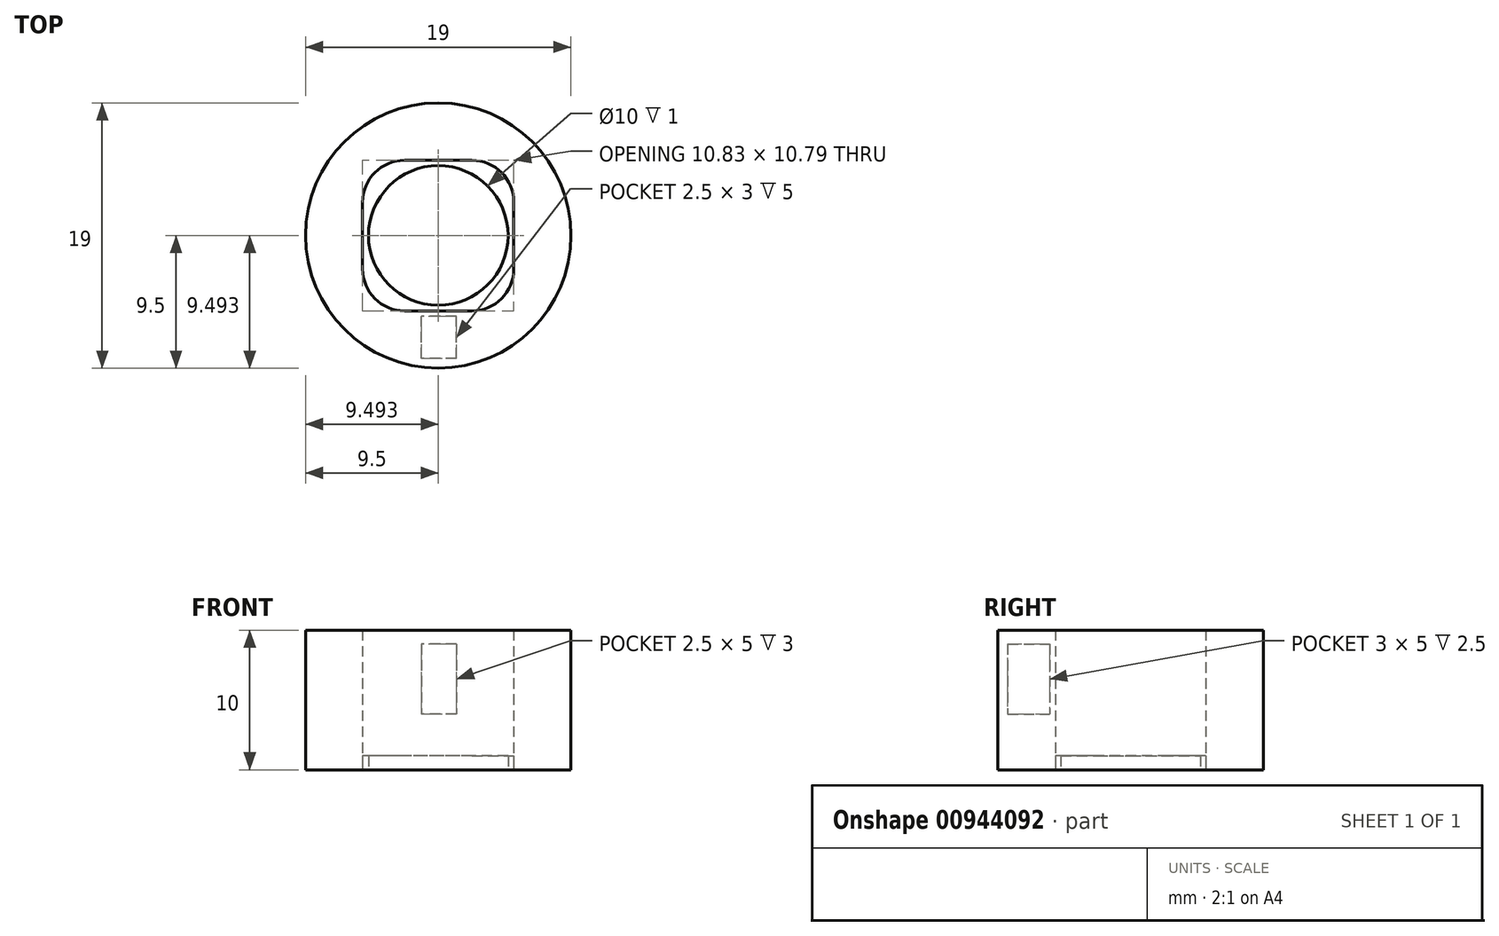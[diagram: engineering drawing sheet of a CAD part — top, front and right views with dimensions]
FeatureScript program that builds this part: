
annotation { "Feature Type Name" : "Feature", "Feature Type Description" : "" }
export const myFeature = defineFeature(function(context is Context, id is Id, definition is map)
    precondition{}
    {
        {
            var Q0;
            Q0=qCreatedBy(makeId("Top.planeOp"),FACE);
            var sketch = newSketch(context, id + "F0", { "sketchPlane" : qUnion([Q0])});
            skCircle(sketch, "E0", {"center": v(0, 0) * mm, "radius": 5 * mm});
            skLineSegment(sketch, "E1.bottom", {"start": v(1.3, -8.8) * mm, "end": v(-1.2, -8.8) * mm});
            skLineSegment(sketch, "E1.top", {"start": v(1.3, -5.8) * mm, "end": v(-1.2, -5.8) * mm});
            skLineSegment(sketch, "E1.left", {"start": v(1.3, -8.8) * mm, "end": v(1.3, -5.8) * mm});
            skLineSegment(sketch, "E1.right", {"start": v(-1.2, -8.8) * mm, "end": v(-1.2, -5.8) * mm});
            skLineSegment(sketch, "E2.bottom", {"start": v(-5.82, -1.25) * mm, "end": v(-8.82, -1.25) * mm});
            skLineSegment(sketch, "E2.top", {"start": v(-5.82, 1.25) * mm, "end": v(-8.82, 1.25) * mm});
            skLineSegment(sketch, "E2.left", {"start": v(-5.82, -1.25) * mm, "end": v(-5.82, 1.25) * mm});
            skLineSegment(sketch, "E2.right", {"start": v(-8.82, -1.25) * mm, "end": v(-8.82, 1.25) * mm});
            skLineSegment(sketch, "E3.bottom", {"start": v(8.8, -1.23) * mm, "end": v(5.8, -1.23) * mm});
            skLineSegment(sketch, "E3.top", {"start": v(8.8, 1.27) * mm, "end": v(5.8, 1.27) * mm});
            skLineSegment(sketch, "E3.left", {"start": v(8.8, -1.23) * mm, "end": v(8.8, 1.27) * mm});
            skLineSegment(sketch, "E3.right", {"start": v(5.8, -1.23) * mm, "end": v(5.8, 1.27) * mm});
            skCircle(sketch, "E4", {"center": v(0, 0) * mm, "radius": 9.5 * mm});
            skLineSegment(sketch, "E5.bottom", {"start": v(1.3, 5.79) * mm, "end": v(-1.2, 5.79) * mm});
            skLineSegment(sketch, "E5.top", {"start": v(1.3, 8.79) * mm, "end": v(-1.2, 8.79) * mm});
            skLineSegment(sketch, "E5.left", {"start": v(1.3, 5.79) * mm, "end": v(1.3, 8.79) * mm});
            skLineSegment(sketch, "E5.right", {"start": v(-1.2, 5.79) * mm, "end": v(-1.2, 8.79) * mm});
            skLineSegment(sketch, "E6.bottom", {"start": v(2.4, -5.4) * mm, "end": v(-2.42, -5.4) * mm});
            skLineSegment(sketch, "E6.top", {"start": v(2.4, 5.39) * mm, "end": v(-2.42, 5.39) * mm});
            skLineSegment(sketch, "E6.left", {"start": v(5.4, -2.4) * mm, "end": v(5.4, 2.39) * mm});
            skLineSegment(sketch, "E6.right", {"start": v(-5.42, -2.4) * mm, "end": v(-5.42, 2.39) * mm});
            skPoint(sketch, "E7.visualSharp", {"position": v(5.4, 5.39) * mm});
            skArc(sketch, "E7.filletArc", {"start": v(5.4, 2.39) * mm, "mid": v(4.53, 4.5) * mm, "end": v(2.4, 5.39) * mm});
            skPoint(sketch, "E8.visualSharp", {"position": v(-5.42, 5.39) * mm});
            skArc(sketch, "E8.filletArc", {"start": v(-2.42, 5.39) * mm, "mid": v(-4.54, 4.5) * mm, "end": v(-5.42, 2.39) * mm});
            skPoint(sketch, "E9.visualSharp", {"position": v(-5.42, -5.4) * mm});
            skArc(sketch, "E9.filletArc", {"start": v(-5.42, -2.4) * mm, "mid": v(-4.54, -4.52) * mm, "end": v(-2.42, -5.4) * mm});
            skPoint(sketch, "E10.visualSharp", {"position": v(5.4, -5.4) * mm});
            skArc(sketch, "E10.filletArc", {"start": v(2.4, -5.4) * mm, "mid": v(4.53, -4.52) * mm, "end": v(5.4, -2.4) * mm});
            skSolve(sketch);
        }
        {
            var Q0;
            Q0=makeQuery(id+"F0.imprint","IMPRINT",FACE,{"disambiguationData":[TD([[makeQuery(id+"F0.imprint","IMPRINT",EDGE,{"derivedFrom":sQuery(id+"F0.wireOp",EDGE,"E1.bottom")}),1.0]])]});
            extrude(context, id + "F1", {"entities" : qUnion([Q0]), "depth" : 9 * mm, "offsetDistance" : 25 * mm});
        }
        {
            var Q0;
            Q0=makeQuery(id+"F0.imprint","IMPRINT",FACE,{"disambiguationData":[TD([[makeQuery(id+"F0.imprint","IMPRINT",EDGE,{"derivedFrom":sQuery(id+"F0.wireOp",EDGE,"E0")}),-1.0]])]});
            var Q1;
            Q1=makeQuery(id+"F0.imprint","IMPRINT",FACE,{"disambiguationData":[TD([[makeQuery(id+"F0.imprint","IMPRINT",EDGE,{"derivedFrom":sQuery(id+"F0.wireOp",EDGE,"E0")}),-1.0]])]});
            var Q2;
            Q2=makeQuery(id+"F0.imprint","IMPRINT",FACE,{"disambiguationData":[TD([[makeQuery(id+"F0.imprint","IMPRINT",EDGE,{"derivedFrom":sQuery(id+"F0.wireOp",EDGE,"E0")}),-1.0]])]});
            var Q3;
            Q3=makeQuery(id+"F0.imprint","IMPRINT",FACE,{"disambiguationData":[TD([[makeQuery(id+"F0.imprint","IMPRINT",EDGE,{"derivedFrom":sQuery(id+"F0.wireOp",EDGE,"E0")}),-1.0]])]});
            extrude(context, id + "F2", {"entities" : qUnion([Q0, Q1, Q2, Q3]), "depth" : 1 * mm, "offsetDistance" : 25 * mm});
        }
        {
            var Q0;
            Q0=makeQuery(id+"F0.imprint","IMPRINT",FACE,{"disambiguationData":[TD([[makeQuery(id+"F0.imprint","IMPRINT",EDGE,{"derivedFrom":sQuery(id+"F0.wireOp",EDGE,"E3.bottom")}),-1.0]])]});
            extrude(context, id + "F3", {"entities" : qUnion([Q0]), "operationType" : NewBodyOperationType.ADD, "depth" : 4 * mm, "offsetDistance" : 25 * mm});
        }
        {
            var Q0;
            Q0=makeQuery(id+"F0.imprint","IMPRINT",FACE,{"disambiguationData":[TD([[makeQuery(id+"F0.imprint","IMPRINT",EDGE,{"derivedFrom":sQuery(id+"F0.wireOp",EDGE,"E5.bottom")}),-1.0]])]});
            extrude(context, id + "F4", {"entities" : qUnion([Q0]), "operationType" : NewBodyOperationType.ADD, "depth" : 4 * mm, "offsetDistance" : 25 * mm});
        }
        {
            var Q0;
            Q0=makeQuery(id+"F0.imprint","IMPRINT",FACE,{"disambiguationData":[TD([[makeQuery(id+"F0.imprint","IMPRINT",EDGE,{"derivedFrom":sQuery(id+"F0.wireOp",EDGE,"E2.bottom")}),-1.0]])]});
            extrude(context, id + "F5", {"entities" : qUnion([Q0]), "operationType" : NewBodyOperationType.ADD, "depth" : 4 * mm, "offsetDistance" : 25 * mm});
        }
        {
            var Q0;
            Q0=makeQuery(id+"F0.imprint","IMPRINT",FACE,{"disambiguationData":[TD([[makeQuery(id+"F0.imprint","IMPRINT",EDGE,{"derivedFrom":sQuery(id+"F0.wireOp",EDGE,"E1.bottom")}),-1.0]])]});
            extrude(context, id + "F6", {"entities" : qUnion([Q0]), "operationType" : NewBodyOperationType.ADD, "depth" : 4 * mm, "offsetDistance" : 25 * mm});
        }
        {
            var Q0;
            Q0=makeQuery(id+"F1.opExtrude","CAP_FACE",FACE,{"disambiguationData":[OSD([sQuery(id+"F0.wireOp",EDGE,"676d06a7-8a10-4542-b558-494a8dc5b941"),sQuery(id+"F0.wireOp",EDGE,"E1.bottom"),sQuery(id+"F0.wireOp",EDGE,"E1.top"),sQuery(id+"F0.wireOp",EDGE,"E1.left"),sQuery(id+"F0.wireOp",EDGE,"E1.right"),sQuery(id+"F0.wireOp",EDGE,"E2.bottom"),sQuery(id+"F0.wireOp",EDGE,"E2.top"),sQuery(id+"F0.wireOp",EDGE,"E2.left"),sQuery(id+"F0.wireOp",EDGE,"E2.right"),sQuery(id+"F0.wireOp",EDGE,"E3.bottom"),sQuery(id+"F0.wireOp",EDGE,"E3.top"),sQuery(id+"F0.wireOp",EDGE,"E3.left"),sQuery(id+"F0.wireOp",EDGE,"E3.right"),sQuery(id+"F0.wireOp",EDGE,"E4"),sQuery(id+"F0.wireOp",EDGE,"4f3f7f32-6085-43bc-9aca-54c7cad2a61b"),sQuery(id+"F0.wireOp",EDGE,"c9501a06-681c-40af-b5da-22ae8357ead1"),sQuery(id+"F0.wireOp",EDGE,"97876365-872f-46b2-8687-91a6985cbe7f"),sQuery(id+"F0.wireOp",EDGE,"dbca472f-2937-4084-81b8-d414c2d73891"),sQuery(id+"F0.wireOp",EDGE,"5df4914b-71c7-4614-91a7-fa8f79216cf9"),sQuery(id+"F0.wireOp",EDGE,"49a88e00-dbe3-4f2c-b9ad-d5971f43cd45"),sQuery(id+"F0.wireOp",EDGE,"c2b55cfa-2f65-4145-b183-51b3a542c01e"),sQuery(id+"F0.wireOp",EDGE,"5ef8c5e7-ef2e-4496-856d-8f5053b71d5c"),sQuery(id+"F0.wireOp",EDGE,"E5.bottom"),sQuery(id+"F0.wireOp",EDGE,"E5.top"),sQuery(id+"F0.wireOp",EDGE,"E5.left"),sQuery(id+"F0.wireOp",EDGE,"E5.right")])],"isStart":false});
            extrude(context, id + "F7", {"entities" : qUnion([Q0]), "depth" : 1 * mm, "offsetDistance" : 25 * mm});
        }
        {
            var Q0;
            Q0=makeQuery(id+"F7.opExtrude","SWEPT_FACE",FACE,{"disambiguationData":[OSD([sQuery(id+"F0.wireOp",EDGE,"E1.bottom")])]});
            extrude(context, id + "F8", {"entities" : qUnion([Q0]), "operationType" : NewBodyOperationType.ADD, "depth" : 3 * mm, "offsetDistance" : 25 * mm});
        }
        {
            var Q0;
            Q0=makeQuery(id+"F7.opExtrude","SWEPT_FACE",FACE,{"disambiguationData":[OSD([sQuery(id+"F0.wireOp",EDGE,"E3.bottom")])]});
            extrude(context, id + "F9", {"entities" : qUnion([Q0]), "operationType" : NewBodyOperationType.ADD, "depth" : 2.5 * mm, "offsetDistance" : 25 * mm});
        }
        {
            var Q0;
            Q0=makeQuery(id+"F7.opExtrude","SWEPT_FACE",FACE,{"disambiguationData":[OSD([sQuery(id+"F0.wireOp",EDGE,"E5.bottom")])]});
            extrude(context, id + "F10", {"entities" : qUnion([Q0]), "operationType" : NewBodyOperationType.ADD, "depth" : 3 * mm, "offsetDistance" : 25 * mm});
        }
        {
            var Q0;
            Q0=makeQuery(id+"F7.opExtrude","SWEPT_FACE",FACE,{"disambiguationData":[OSD([sQuery(id+"F0.wireOp",EDGE,"E2.bottom")])]});
            extrude(context, id + "F11", {"entities" : qUnion([Q0]), "operationType" : NewBodyOperationType.ADD, "depth" : 2.5 * mm, "offsetDistance" : 25 * mm});
        }
    });
